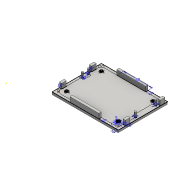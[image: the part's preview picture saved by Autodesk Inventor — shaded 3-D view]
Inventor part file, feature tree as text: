
AUTODESK INVENTOR PART (.ipt)
format: ipt  version: 2016 (Build 200138000, 138)  size: 356,352 bytes
history: native  units: mm
features: extrude x4, other x2, fillet x2, sketch x1, hole x1, pattern_linear x1
ambient origin geometry x8: Origin, YZ Plane, XZ Plane, XY Plane, X Axis, Y Axis, Z Axis, Center Point
bodies: Solid1 (feature_tree)
feature tree (11):
  sketch  "Sketch1"  dims[d9=60.0mm d10=5.0mm d11=5.0mm d14=5.0mm d15=0.0mm d36=0.5mm d44=3.0mm d45=3.0mm d46=3.0mm d47=3.0mm d48=3.0mm d49=3.0mm d50=3.0mm d51=3.0mm d52=10.0mm d53=10.0mm d56=10.0mm d57=10.0mm d58=0.0mm d59=0.5mm d62=5.0mm d63=2.85mm d64=1.0mm d65=60.0mm d67=360.0deg d69=2.3mm d70=0.0mm d71=5.0mm d72=10.0mm d73=0.0mm d74=20.0mm d76=72.0mm d77=20.0mm d79=107.0mm]
  hole  "HOLES1"  [1 undecoded]
  other  "OUTLINE1"
  other  "OUTLINE2"
  extrude  "Extrusion2"  Depth=5.0mm
  fillet  "Fillet1"  Radius=5.0mm
  extrude  "Extrusion7"  Depth=0.5mm
  fillet  "Fillet3"  Radius=3.0mm
  extrude  "Extrusion8"  Depth=3.0mm
  extrude  "Extrusion9"  Depth=3.0mm
  pattern_linear  "Rectangular Pattern2"  Spacing1=3.0mm  [1 undecoded]
note: 2 required parameter values undecoded (feature->parameter linkage not recoverable at this tier; creation-order binding heuristic only, values carry confidence <= 0.55)
